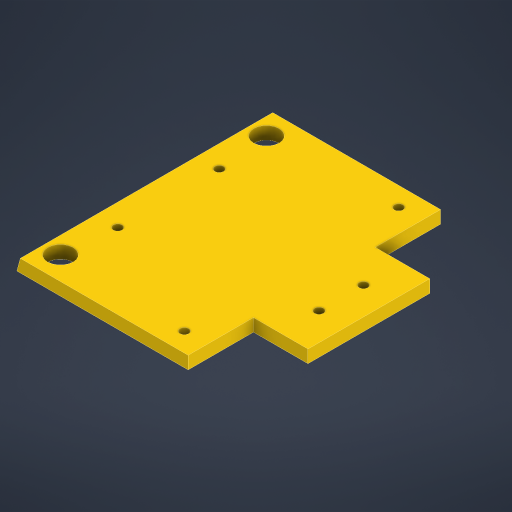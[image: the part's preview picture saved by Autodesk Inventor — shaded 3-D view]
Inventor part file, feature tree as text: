
AUTODESK INVENTOR PART (.ipt)
format: ipt  version: 2024 (Build 280153000, 153)  size: 238,080 bytes
history: native  units: mm
features: sketch x2, extrude x2, other x1, hole x1
ambient origin geometry x8: Origin, YZ Plane, XZ Plane, XY Plane, X Axis, Y Axis, Z Axis, Center Point
bodies: Body1 (feature_tree)
feature tree (6):
  other  "Těleso1"
  sketch  "Náčrt1"
  extrude  "Vysunutí1"  Depth=99.5mm
  extrude  "Vysunutí2"  Depth=99.5mm
  hole  "Díra1"  [1 undecoded]
  sketch  "Náčrt2"
note: 1 required parameter value undecoded (feature->parameter linkage not recoverable at this tier; creation-order binding heuristic only, values carry confidence <= 0.55)
